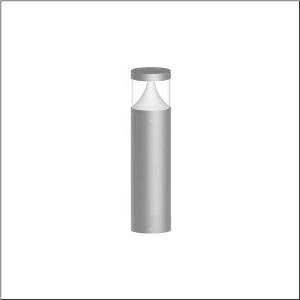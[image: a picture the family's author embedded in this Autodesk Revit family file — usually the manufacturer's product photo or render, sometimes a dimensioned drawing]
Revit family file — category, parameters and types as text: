
# Revit family: cl_31_poller_60_5cl434603
name_source: partatom
category: Lighting Fixtures
units: mm (PartAtom-declared; Revit-internal decimal feet)

## family parameters
Cut with Voids When Loaded = No
Host = Face
Light Source = No
Part Type = Normal
Room Calculation Point = No
Round Connector Dimension = Use Diameter
Shared = No

## types (1)
- --- (1 x LED, 1500 lm, 14 W, 3000K)
    Apparent Load = 14 VA
    CIE Flux Codes = 19 66 88 92 100
    Color Rendering = 80
    Color Temperature = 3000K
    Default Elevation = 1800 mm
    Description = CL 31 Bollard 60, bollard luminaire, primary light control with lens, of PC, primary optical cover: cover panel, of PC, transparent, secondary light control with reflector, of PC, primary light characteristic: asymmetric, LED, rated luminous flux: 1.500lm, luminous efficacy: 107lm/W, light colour: 830, colour temperature: 3000K, control gear: DALI, with terminal, 5-pole, max. 2.5mm², mains connection: 220..240V, AC, 50/60Hz, rated input power: 14W, luminaire housing, of aluminium, powder-coated, SITECO metallic grey, diameter: 170mm, height: 600mm, protection rating (complete): IP65, insulation class (complete): insulation class I (protective earthing), certification: CE, ENEC, impact resistance: IK10, permissible operating ambient temperature for outdoor applications: -20..+50°C, packaging unit: 1 piece
    Height = 200 mm  [stored 0.656168 ft]
    Lamp = 1 x LED
    Lamp Light Flux = 1500 lm
    Lamp Power = 14 W
    Lamp count = 1
    Length = 170 mm  [stored 0.557743 ft]
    Luminous efficacy = 107 lm/W
    Manufacturer = Siteco
    ModVariant = No
    Model = 5CL434603
    Mounting Place = Floor
    Mounting Type = Freestanding
    Number of Poles = 1
    OnlyDefault = Yes
    Power Factor = 1
    Product Name = CL 31 Poller 60
    Product group = bollard luminaire
    ProductGroupID = 1304
    Protection Class = Protection class I
    Protection Degree = IP 65
    RLX_Detail_Level = 1
    RLX_Emergency_Light_Flux = 0 lm
    RLX_Emergency_Type = 0
    RLX_Emergency_Type_DB = No
    RlxData = <blob elided: 63789 chars, md5=beaba10f>
    Socket = socket
    Standby Power = 0 W
    System Light Flux = 1500 lm
    System Power = 14 W
    Type Comments = factory setting: luminous flux: 100 % | dim-lin: 254 | 350 mA
    Type Image = l_1006903.jpg
    URL = http://relux.com
    VarID = @adj_192739
    Voltage = 0 V
    Weight = 0.00 kg
    Width = 0 mm  [stored 0 ft]

note: [stored X ft] marks values corroborated as IEEE doubles in the binary element streams (Revit-internal decimal feet)

## geometry (parser evidence)
native form markers: Blend x4, Sweep x12
no freeform markers — native parametric forms only
